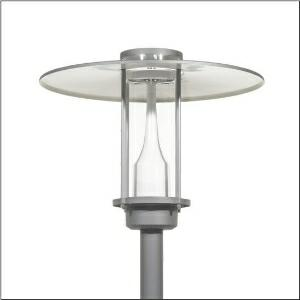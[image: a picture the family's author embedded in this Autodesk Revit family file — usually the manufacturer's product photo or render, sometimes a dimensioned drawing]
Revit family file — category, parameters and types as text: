
# Revit family: city-light_plus_iq___p1_0a_5xa5275ff14h000022_8535
name_source: partatom
category: Lighting Fixtures
units: mm (PartAtom-declared; Revit-internal decimal feet)

## family parameters
Cut with Voids When Loaded = No
Host = Face
Light Source = No
Part Type = Normal
Room Calculation Point = No
Round Connector Dimension = Use Diameter
Shared = No

## types (1)
- --- (1 x LED, 1440 lm, 10.5 W, 3000K)
    Apparent Load = 11 VA
    CIE Flux Codes = 32 61 90 96 100
    Color Rendering = 70
    Color Temperature = 3000K
    Default Elevation = 1800 mm
    Description = City-Light Plus iQ, mast luminaire, Module 540 iQ-SR, primary light control with 3 zone facetted reflector, of plastic, silver coated, highly specular, structured, primary optical cover: cover, of PMMA, transparent, light distribution: P1.0a, light emission: direct distribution, primary light characteristic: strongly asymmetric, installation type: post-top, LED, High Power LED, rated luminous flux: 1.440lm, luminous efficacy: 137lm/W, light colour: 730, colour temperature: 3000K, control gear: iQ Street-Remote, control: Street-Remote, Auto-Match, Temp-Guard, Lumen-Switch, Night-Set, Smart-Wire, Light-Fading, Desk-Remote (wireless, voltage-free reading and setting of iQ features in the workshop via application-optimized NFC function/RFID function), optimised constant luminous flux control (CLO 2.0), pre-setting: logarithmic dimming characteristic, mains connection: 230..240V, AC, 50/60Hz, connection cable pre-assembled, cable length: 5,5m, wiring characteristics: H07RN-F, start of lifetime: 11W, end of service life: 11W, reduction: 5W, luminaire housing, upper part, of glass-fibre reinforced polyester, coated, SITECO metallic grey (DB 702S), diameter: 750mm, height: 590mm, spigot size: d x l = 76 x 70mm (post-top) | with reducer (optional accessory) 60 x 70mm, mounting height: 3..5m, post-top mast mounting element, of diecast aluminium, coated, SITECO metallic grey (DB 702S), Module 540 iQ-SR, traffic white (RAL 9016), equipment: standard, protection rating (complete): IP65, insulation class (complete): insulation class II (safety insulation), certification: CE, ENEC, VDE, packaging unit: 1 piece

Light Distribution: P1.0a
    Height = 590 mm
    Lamp = 1 x LED
    Lamp Light Flux = 1440 lm
    Lamp Power = 10.5 W
    Lamp count = 1
    Length = 750 mm
    Luminous efficacy = 137 lm/W
    Manufacturer = Siteco
    ModVariant = No
    Model = 5XA5275FF14H000022
    Number of Poles = 1
    OnlyDefault = Yes
    Power Factor = 1
    Product Name = City-Light Plus iQ | P1.0a
    Product group = mast luminaire | pylon top
    ProductGroupID = 6100
    Protection Class = Protection class II
    Protection Degree = IP 65
    RLX_Detail_Level = 1
    RLX_Emergency_Light_Flux = 0 lm
    RLX_Emergency_Type = 0
    RLX_Emergency_Type_DB = No
    RlxData = <blob elided: 51713 chars, md5=c84fb51d>
    Socket = socket
    Standby Power = 0 W
    System Light Flux = 1440 lm
    System Power = 11 W
    Type Comments = factory setting: luminous flux: 100 % | dim-lin: 254 | 419 mA
    Type Image = l_1006456.jpg
    URL = http://relux.com
    VarID = @adj_159399
    Voltage = 0 V
    Weight = 0.00 kg
    Width = 0 mm  [stored 0 ft]

note: [stored X ft] marks values corroborated as IEEE doubles in the binary element streams (Revit-internal decimal feet)

## geometry (parser evidence)
native form markers: Blend x4, Sweep x9
no freeform markers — native parametric forms only
